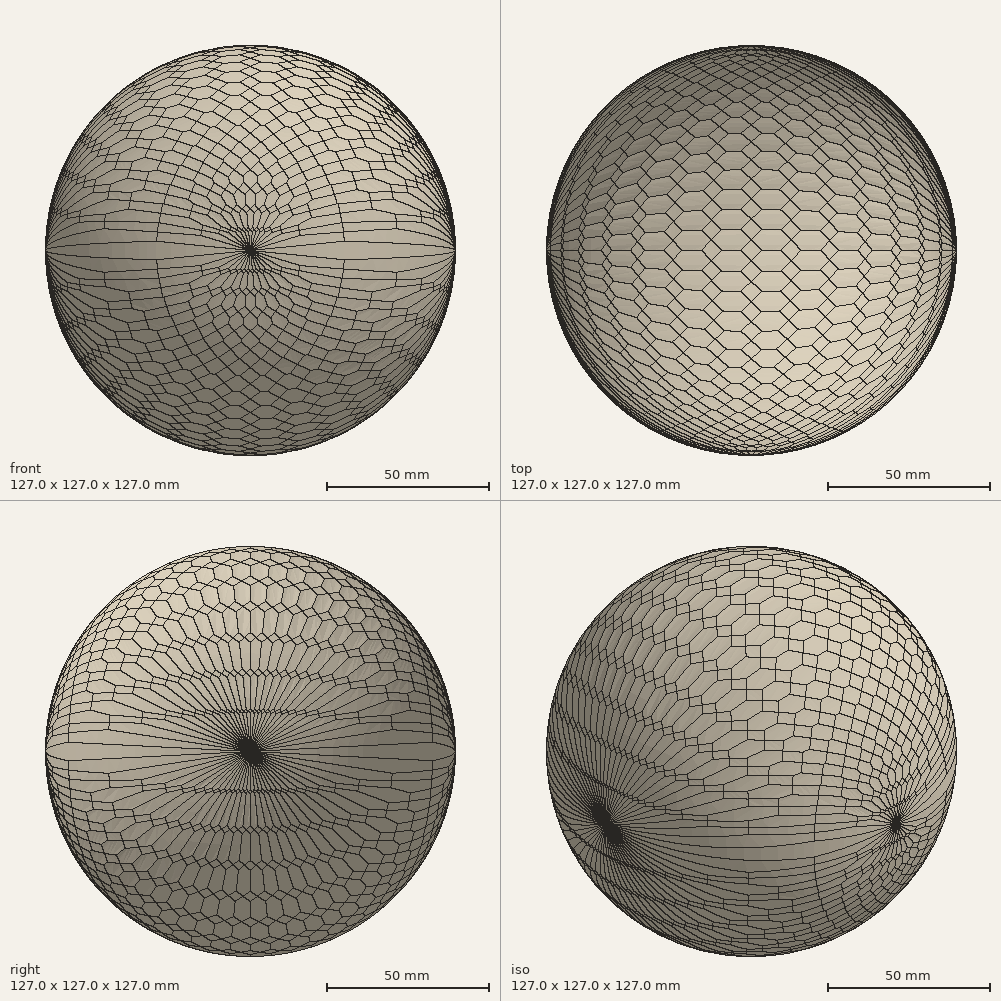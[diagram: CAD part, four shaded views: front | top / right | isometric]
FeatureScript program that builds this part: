
annotation { "Feature Type Name" : "Feature", "Feature Type Description" : "" }
export const myFeature = defineFeature(function(context is Context, id is Id, definition is map)
    precondition{}
    {
        {
            var Q0;
            Q0=qCreatedBy(makeId("Top.planeOp"),FACE);
            var sketch = newSketch(context, id + "F0", { "sketchPlane" : qUnion([Q0])});
            skCircle(sketch, "E0", {"center": v(0, 0) * mm, "radius": 63.5 * mm});
            skLineSegment(sketch, "E1", {"start": v(0, 63.5) * mm, "end": v(0, -63.5) * mm});
            skLineSegment(sketch, "E2", {"start": v(-63.5, 0) * mm, "end": v(63.5, 0) * mm});
            skSolve(sketch);
        }
        {
            var Q0;
            {var subQ0=sQuery(id+"F0.wireOp",EDGE,"E1");var subQ1=sQuery(id+"F0.wireOp",EDGE,"E0");var subQ2=makeQuery(id+"F0.imprint","INTERSECT",VERTEX,{"disambiguationData":[OD(0.0)],"derivedFrom":[subQ1,subQ0]});Q0=makeQuery(id+"F0.imprint","IMPRINT",FACE,{"disambiguationData":[TD([[makeQuery(id+"F0.imprint","IMPRINT",EDGE,{"disambiguationData":[TD([[subQ2,-1.0]])],"derivedFrom":subQ1}),1.0]])]});}
            var Q1;
            {var subQ0=sQuery(id+"F0.wireOp",EDGE,"E1");var subQ1=sQuery(id+"F0.wireOp",EDGE,"E0");var subQ2=makeQuery(id+"F0.imprint","INTERSECT",VERTEX,{"disambiguationData":[OD(0.0)],"derivedFrom":[subQ1,subQ0]});Q1=makeQuery(id+"F0.imprint","IMPRINT",FACE,{"disambiguationData":[TD([[makeQuery(id+"F0.imprint","IMPRINT",EDGE,{"disambiguationData":[TD([[subQ2,1.0]])],"derivedFrom":subQ1}),1.0]])]});}
            var Q2;
            {var subQ0=sQuery(id+"F0.wireOp",EDGE,"E1");var subQ1=sQuery(id+"F0.wireOp",EDGE,"E0");var subQ2=makeQuery(id+"F0.imprint","INTERSECT",VERTEX,{"disambiguationData":[OD(1.0)],"derivedFrom":[subQ1,subQ0]});Q2=makeQuery(id+"F0.imprint","IMPRINT",FACE,{"disambiguationData":[TD([[makeQuery(id+"F0.imprint","IMPRINT",EDGE,{"disambiguationData":[TD([[subQ2,-1.0]])],"derivedFrom":subQ1}),1.0]])]});}
            var Q3;
            {var subQ0=sQuery(id+"F0.wireOp",EDGE,"E1");var subQ1=sQuery(id+"F0.wireOp",EDGE,"E0");var subQ2=makeQuery(id+"F0.imprint","INTERSECT",VERTEX,{"disambiguationData":[OD(1.0)],"derivedFrom":[subQ1,subQ0]});Q3=makeQuery(id+"F0.imprint","IMPRINT",FACE,{"disambiguationData":[TD([[makeQuery(id+"F0.imprint","IMPRINT",EDGE,{"disambiguationData":[TD([[subQ2,1.0]])],"derivedFrom":subQ1}),1.0]])]});}
            extrude(context, id + "F1", {"entities" : qUnion([Q0, Q1, Q2, Q3]), "depth" : 279.4 * mm, "offsetDistance" : 25.4 * mm});
        }
        {
            var Q0;
            Q0=makeQuery(id+"F1.opExtrude","CAP_FACE",FACE,{"disambiguationData":[OSD([sQuery(id+"F0.wireOp",EDGE,"E0")])],"isStart":true});
            extrude(context, id + "F2", {"entities" : qUnion([Q0]), "operationType" : NewBodyOperationType.ADD, "depth" : 279.4 * mm, "offsetDistance" : 25.4 * mm});
        }
        {
            var Q0;
            Q0=makeQuery(id+"F1.opExtrude","SWEPT_BODY",BODY,{"disambiguationData":[OSD([sQuery(id+"F0.wireOp",EDGE,"E0")])]});
            var Q1;
            Q1=sQuery(id+"F0.wireOp",EDGE,"E2");
            circularPattern(context, id + "F3", {"entities" : qUnion([Q0]), "axis" : qUnion([Q1]), "angle" : 180 * degree, "instanceCount" : 32, "equalSpace" : true});
        }
        {
            var Q0;
            Q0=makeQuery(id+"F1.opExtrude","SWEPT_BODY",BODY,{"disambiguationData":[OSD([sQuery(id+"F0.wireOp",EDGE,"E0")])]});
            var Q1;
            Q1=sQuery(id+"F0.wireOp",EDGE,"E1");
            circularPattern(context, id + "F4", {"entities" : qUnion([Q0]), "axis" : qUnion([Q1]), "angle" : 360 * degree, "instanceCount" : 32, "equalSpace" : true});
        }
        {
            var Q0;
            Q0=makeQuery(id+"F1.opExtrude","SWEPT_BODY",BODY,{"disambiguationData":[OSD([sQuery(id+"F0.wireOp",EDGE,"E0")])]});
            var Q1;
            Q1=makeQuery(id+"F3.opPattern","COPY",BODY,{"derivedFrom":makeQuery(id+"F1.opExtrude","SWEPT_BODY",BODY,{"disambiguationData":[OSD([sQuery(id+"F0.wireOp",EDGE,"E0")])]}),"instanceName":"2"});
            var Q2;
            Q2=makeQuery(id+"F3.opPattern","COPY",BODY,{"derivedFrom":makeQuery(id+"F1.opExtrude","SWEPT_BODY",BODY,{"disambiguationData":[OSD([sQuery(id+"F0.wireOp",EDGE,"E0")])]}),"instanceName":"7"});
            var Q3;
            Q3=makeQuery(id+"F3.opPattern","COPY",BODY,{"derivedFrom":makeQuery(id+"F1.opExtrude","SWEPT_BODY",BODY,{"disambiguationData":[OSD([sQuery(id+"F0.wireOp",EDGE,"E0")])]}),"instanceName":"15"});
            var Q4;
            Q4=makeQuery(id+"F4.opPattern","COPY",BODY,{"derivedFrom":makeQuery(id+"F1.opExtrude","SWEPT_BODY",BODY,{"disambiguationData":[OSD([sQuery(id+"F0.wireOp",EDGE,"E0")])]}),"instanceName":"1"});
            var Q5;
            Q5=makeQuery(id+"F4.opPattern","COPY",BODY,{"derivedFrom":makeQuery(id+"F1.opExtrude","SWEPT_BODY",BODY,{"disambiguationData":[OSD([sQuery(id+"F0.wireOp",EDGE,"E0")])]}),"instanceName":"5"});
            var Q6;
            Q6=makeQuery(id+"F4.opPattern","COPY",BODY,{"derivedFrom":makeQuery(id+"F1.opExtrude","SWEPT_BODY",BODY,{"disambiguationData":[OSD([sQuery(id+"F0.wireOp",EDGE,"E0")])]}),"instanceName":"12"});
            var Q7;
            Q7=makeQuery(id+"F4.opPattern","COPY",BODY,{"derivedFrom":makeQuery(id+"F1.opExtrude","SWEPT_BODY",BODY,{"disambiguationData":[OSD([sQuery(id+"F0.wireOp",EDGE,"E0")])]}),"instanceName":"11"});
            var Q8;
            Q8=makeQuery(id+"F4.opPattern","COPY",BODY,{"derivedFrom":makeQuery(id+"F1.opExtrude","SWEPT_BODY",BODY,{"disambiguationData":[OSD([sQuery(id+"F0.wireOp",EDGE,"E0")])]}),"instanceName":"13"});
            var Q9;
            Q9=makeQuery(id+"F4.opPattern","COPY",BODY,{"derivedFrom":makeQuery(id+"F1.opExtrude","SWEPT_BODY",BODY,{"disambiguationData":[OSD([sQuery(id+"F0.wireOp",EDGE,"E0")])]}),"instanceName":"14"});
            var Q10;
            Q10=makeQuery(id+"F4.opPattern","COPY",BODY,{"derivedFrom":makeQuery(id+"F1.opExtrude","SWEPT_BODY",BODY,{"disambiguationData":[OSD([sQuery(id+"F0.wireOp",EDGE,"E0")])]}),"instanceName":"3"});
            var Q11;
            Q11=makeQuery(id+"F4.opPattern","COPY",BODY,{"derivedFrom":makeQuery(id+"F1.opExtrude","SWEPT_BODY",BODY,{"disambiguationData":[OSD([sQuery(id+"F0.wireOp",EDGE,"E0")])]}),"instanceName":"6"});
            var Q12;
            Q12=makeQuery(id+"F4.opPattern","COPY",BODY,{"derivedFrom":makeQuery(id+"F1.opExtrude","SWEPT_BODY",BODY,{"disambiguationData":[OSD([sQuery(id+"F0.wireOp",EDGE,"E0")])]}),"instanceName":"8"});
            var Q13;
            Q13=makeQuery(id+"F4.opPattern","COPY",BODY,{"derivedFrom":makeQuery(id+"F1.opExtrude","SWEPT_BODY",BODY,{"disambiguationData":[OSD([sQuery(id+"F0.wireOp",EDGE,"E0")])]}),"instanceName":"7"});
            var Q14;
            Q14=makeQuery(id+"F4.opPattern","COPY",BODY,{"derivedFrom":makeQuery(id+"F1.opExtrude","SWEPT_BODY",BODY,{"disambiguationData":[OSD([sQuery(id+"F0.wireOp",EDGE,"E0")])]}),"instanceName":"4"});
            var Q15;
            Q15=makeQuery(id+"F3.opPattern","COPY",BODY,{"derivedFrom":makeQuery(id+"F1.opExtrude","SWEPT_BODY",BODY,{"disambiguationData":[OSD([sQuery(id+"F0.wireOp",EDGE,"E0")])]}),"instanceName":"13"});
            var Q16;
            Q16=makeQuery(id+"F3.opPattern","COPY",BODY,{"derivedFrom":makeQuery(id+"F1.opExtrude","SWEPT_BODY",BODY,{"disambiguationData":[OSD([sQuery(id+"F0.wireOp",EDGE,"E0")])]}),"instanceName":"14"});
            var Q17;
            Q17=makeQuery(id+"F3.opPattern","COPY",BODY,{"derivedFrom":makeQuery(id+"F1.opExtrude","SWEPT_BODY",BODY,{"disambiguationData":[OSD([sQuery(id+"F0.wireOp",EDGE,"E0")])]}),"instanceName":"12"});
            var Q18;
            Q18=makeQuery(id+"F3.opPattern","COPY",BODY,{"derivedFrom":makeQuery(id+"F1.opExtrude","SWEPT_BODY",BODY,{"disambiguationData":[OSD([sQuery(id+"F0.wireOp",EDGE,"E0")])]}),"instanceName":"11"});
            var Q19;
            Q19=makeQuery(id+"F4.opPattern","COPY",BODY,{"derivedFrom":makeQuery(id+"F1.opExtrude","SWEPT_BODY",BODY,{"disambiguationData":[OSD([sQuery(id+"F0.wireOp",EDGE,"E0")])]}),"instanceName":"10"});
            var Q20;
            Q20=makeQuery(id+"F3.opPattern","COPY",BODY,{"derivedFrom":makeQuery(id+"F1.opExtrude","SWEPT_BODY",BODY,{"disambiguationData":[OSD([sQuery(id+"F0.wireOp",EDGE,"E0")])]}),"instanceName":"20"});
            var Q21;
            Q21=makeQuery(id+"F3.opPattern","COPY",BODY,{"derivedFrom":makeQuery(id+"F1.opExtrude","SWEPT_BODY",BODY,{"disambiguationData":[OSD([sQuery(id+"F0.wireOp",EDGE,"E0")])]}),"instanceName":"18"});
            var Q22;
            Q22=makeQuery(id+"F3.opPattern","COPY",BODY,{"derivedFrom":makeQuery(id+"F1.opExtrude","SWEPT_BODY",BODY,{"disambiguationData":[OSD([sQuery(id+"F0.wireOp",EDGE,"E0")])]}),"instanceName":"17"});
            var Q23;
            Q23=makeQuery(id+"F3.opPattern","COPY",BODY,{"derivedFrom":makeQuery(id+"F1.opExtrude","SWEPT_BODY",BODY,{"disambiguationData":[OSD([sQuery(id+"F0.wireOp",EDGE,"E0")])]}),"instanceName":"21"});
            var Q24;
            Q24=makeQuery(id+"F4.opPattern","COPY",BODY,{"derivedFrom":makeQuery(id+"F1.opExtrude","SWEPT_BODY",BODY,{"disambiguationData":[OSD([sQuery(id+"F0.wireOp",EDGE,"E0")])]}),"instanceName":"16"});
            var Q25;
            Q25=makeQuery(id+"F4.opPattern","COPY",BODY,{"derivedFrom":makeQuery(id+"F1.opExtrude","SWEPT_BODY",BODY,{"disambiguationData":[OSD([sQuery(id+"F0.wireOp",EDGE,"E0")])]}),"instanceName":"24"});
            var Q26;
            Q26=makeQuery(id+"F4.opPattern","COPY",BODY,{"derivedFrom":makeQuery(id+"F1.opExtrude","SWEPT_BODY",BODY,{"disambiguationData":[OSD([sQuery(id+"F0.wireOp",EDGE,"E0")])]}),"instanceName":"28"});
            var Q27;
            Q27=makeQuery(id+"F4.opPattern","COPY",BODY,{"derivedFrom":makeQuery(id+"F1.opExtrude","SWEPT_BODY",BODY,{"disambiguationData":[OSD([sQuery(id+"F0.wireOp",EDGE,"E0")])]}),"instanceName":"27"});
            var Q28;
            Q28=makeQuery(id+"F4.opPattern","COPY",BODY,{"derivedFrom":makeQuery(id+"F1.opExtrude","SWEPT_BODY",BODY,{"disambiguationData":[OSD([sQuery(id+"F0.wireOp",EDGE,"E0")])]}),"instanceName":"20"});
            var Q29;
            Q29=makeQuery(id+"F3.opPattern","COPY",BODY,{"derivedFrom":makeQuery(id+"F1.opExtrude","SWEPT_BODY",BODY,{"disambiguationData":[OSD([sQuery(id+"F0.wireOp",EDGE,"E0")])]}),"instanceName":"27"});
            var Q30;
            Q30=makeQuery(id+"F4.opPattern","COPY",BODY,{"derivedFrom":makeQuery(id+"F1.opExtrude","SWEPT_BODY",BODY,{"disambiguationData":[OSD([sQuery(id+"F0.wireOp",EDGE,"E0")])]}),"instanceName":"31"});
            var Q31;
            Q31=makeQuery(id+"F4.opPattern","COPY",BODY,{"derivedFrom":makeQuery(id+"F1.opExtrude","SWEPT_BODY",BODY,{"disambiguationData":[OSD([sQuery(id+"F0.wireOp",EDGE,"E0")])]}),"instanceName":"30"});
            var Q32;
            Q32=makeQuery(id+"F4.opPattern","COPY",BODY,{"derivedFrom":makeQuery(id+"F1.opExtrude","SWEPT_BODY",BODY,{"disambiguationData":[OSD([sQuery(id+"F0.wireOp",EDGE,"E0")])]}),"instanceName":"25"});
            var Q33;
            Q33=makeQuery(id+"F4.opPattern","COPY",BODY,{"derivedFrom":makeQuery(id+"F1.opExtrude","SWEPT_BODY",BODY,{"disambiguationData":[OSD([sQuery(id+"F0.wireOp",EDGE,"E0")])]}),"instanceName":"18"});
            var Q34;
            Q34=makeQuery(id+"F3.opPattern","COPY",BODY,{"derivedFrom":makeQuery(id+"F1.opExtrude","SWEPT_BODY",BODY,{"disambiguationData":[OSD([sQuery(id+"F0.wireOp",EDGE,"E0")])]}),"instanceName":"24"});
            var Q35;
            Q35=makeQuery(id+"F4.opPattern","COPY",BODY,{"derivedFrom":makeQuery(id+"F1.opExtrude","SWEPT_BODY",BODY,{"disambiguationData":[OSD([sQuery(id+"F0.wireOp",EDGE,"E0")])]}),"instanceName":"21"});
            var Q36;
            Q36=makeQuery(id+"F4.opPattern","COPY",BODY,{"derivedFrom":makeQuery(id+"F1.opExtrude","SWEPT_BODY",BODY,{"disambiguationData":[OSD([sQuery(id+"F0.wireOp",EDGE,"E0")])]}),"instanceName":"23"});
            var Q37;
            Q37=makeQuery(id+"F4.opPattern","COPY",BODY,{"derivedFrom":makeQuery(id+"F1.opExtrude","SWEPT_BODY",BODY,{"disambiguationData":[OSD([sQuery(id+"F0.wireOp",EDGE,"E0")])]}),"instanceName":"22"});
            var Q38;
            Q38=makeQuery(id+"F3.opPattern","COPY",BODY,{"derivedFrom":makeQuery(id+"F1.opExtrude","SWEPT_BODY",BODY,{"disambiguationData":[OSD([sQuery(id+"F0.wireOp",EDGE,"E0")])]}),"instanceName":"22"});
            var Q39;
            Q39=makeQuery(id+"F3.opPattern","COPY",BODY,{"derivedFrom":makeQuery(id+"F1.opExtrude","SWEPT_BODY",BODY,{"disambiguationData":[OSD([sQuery(id+"F0.wireOp",EDGE,"E0")])]}),"instanceName":"16"});
            var Q40;
            Q40=makeQuery(id+"F3.opPattern","COPY",BODY,{"derivedFrom":makeQuery(id+"F1.opExtrude","SWEPT_BODY",BODY,{"disambiguationData":[OSD([sQuery(id+"F0.wireOp",EDGE,"E0")])]}),"instanceName":"23"});
            var Q41;
            Q41=makeQuery(id+"F3.opPattern","COPY",BODY,{"derivedFrom":makeQuery(id+"F1.opExtrude","SWEPT_BODY",BODY,{"disambiguationData":[OSD([sQuery(id+"F0.wireOp",EDGE,"E0")])]}),"instanceName":"25"});
            var Q42;
            Q42=makeQuery(id+"F3.opPattern","COPY",BODY,{"derivedFrom":makeQuery(id+"F1.opExtrude","SWEPT_BODY",BODY,{"disambiguationData":[OSD([sQuery(id+"F0.wireOp",EDGE,"E0")])]}),"instanceName":"30"});
            var Q43;
            Q43=makeQuery(id+"F4.opPattern","COPY",BODY,{"derivedFrom":makeQuery(id+"F1.opExtrude","SWEPT_BODY",BODY,{"disambiguationData":[OSD([sQuery(id+"F0.wireOp",EDGE,"E0")])]}),"instanceName":"26"});
            var Q44;
            Q44=makeQuery(id+"F4.opPattern","COPY",BODY,{"derivedFrom":makeQuery(id+"F1.opExtrude","SWEPT_BODY",BODY,{"disambiguationData":[OSD([sQuery(id+"F0.wireOp",EDGE,"E0")])]}),"instanceName":"9"});
            var Q45;
            Q45=makeQuery(id+"F4.opPattern","COPY",BODY,{"derivedFrom":makeQuery(id+"F1.opExtrude","SWEPT_BODY",BODY,{"disambiguationData":[OSD([sQuery(id+"F0.wireOp",EDGE,"E0")])]}),"instanceName":"29"});
            var Q46;
            Q46=makeQuery(id+"F4.opPattern","COPY",BODY,{"derivedFrom":makeQuery(id+"F1.opExtrude","SWEPT_BODY",BODY,{"disambiguationData":[OSD([sQuery(id+"F0.wireOp",EDGE,"E0")])]}),"instanceName":"19"});
            var Q47;
            Q47=makeQuery(id+"F4.opPattern","COPY",BODY,{"derivedFrom":makeQuery(id+"F1.opExtrude","SWEPT_BODY",BODY,{"disambiguationData":[OSD([sQuery(id+"F0.wireOp",EDGE,"E0")])]}),"instanceName":"17"});
            var Q48;
            Q48=makeQuery(id+"F3.opPattern","COPY",BODY,{"derivedFrom":makeQuery(id+"F1.opExtrude","SWEPT_BODY",BODY,{"disambiguationData":[OSD([sQuery(id+"F0.wireOp",EDGE,"E0")])]}),"instanceName":"4"});
            var Q49;
            Q49=makeQuery(id+"F3.opPattern","COPY",BODY,{"derivedFrom":makeQuery(id+"F1.opExtrude","SWEPT_BODY",BODY,{"disambiguationData":[OSD([sQuery(id+"F0.wireOp",EDGE,"E0")])]}),"instanceName":"19"});
            var Q50;
            Q50=makeQuery(id+"F3.opPattern","COPY",BODY,{"derivedFrom":makeQuery(id+"F1.opExtrude","SWEPT_BODY",BODY,{"disambiguationData":[OSD([sQuery(id+"F0.wireOp",EDGE,"E0")])]}),"instanceName":"26"});
            var Q51;
            Q51=makeQuery(id+"F3.opPattern","COPY",BODY,{"derivedFrom":makeQuery(id+"F1.opExtrude","SWEPT_BODY",BODY,{"disambiguationData":[OSD([sQuery(id+"F0.wireOp",EDGE,"E0")])]}),"instanceName":"9"});
            var Q52;
            Q52=makeQuery(id+"F3.opPattern","COPY",BODY,{"derivedFrom":makeQuery(id+"F1.opExtrude","SWEPT_BODY",BODY,{"disambiguationData":[OSD([sQuery(id+"F0.wireOp",EDGE,"E0")])]}),"instanceName":"31"});
            var Q53;
            Q53=makeQuery(id+"F3.opPattern","COPY",BODY,{"derivedFrom":makeQuery(id+"F1.opExtrude","SWEPT_BODY",BODY,{"disambiguationData":[OSD([sQuery(id+"F0.wireOp",EDGE,"E0")])]}),"instanceName":"5"});
            var Q54;
            Q54=makeQuery(id+"F3.opPattern","COPY",BODY,{"derivedFrom":makeQuery(id+"F1.opExtrude","SWEPT_BODY",BODY,{"disambiguationData":[OSD([sQuery(id+"F0.wireOp",EDGE,"E0")])]}),"instanceName":"8"});
            var Q55;
            Q55=makeQuery(id+"F3.opPattern","COPY",BODY,{"derivedFrom":makeQuery(id+"F1.opExtrude","SWEPT_BODY",BODY,{"disambiguationData":[OSD([sQuery(id+"F0.wireOp",EDGE,"E0")])]}),"instanceName":"10"});
            var Q56;
            Q56=makeQuery(id+"F3.opPattern","COPY",BODY,{"derivedFrom":makeQuery(id+"F1.opExtrude","SWEPT_BODY",BODY,{"disambiguationData":[OSD([sQuery(id+"F0.wireOp",EDGE,"E0")])]}),"instanceName":"6"});
            var Q57;
            Q57=makeQuery(id+"F4.opPattern","COPY",BODY,{"derivedFrom":makeQuery(id+"F1.opExtrude","SWEPT_BODY",BODY,{"disambiguationData":[OSD([sQuery(id+"F0.wireOp",EDGE,"E0")])]}),"instanceName":"15"});
            var Q58;
            Q58=makeQuery(id+"F3.opPattern","COPY",BODY,{"derivedFrom":makeQuery(id+"F1.opExtrude","SWEPT_BODY",BODY,{"disambiguationData":[OSD([sQuery(id+"F0.wireOp",EDGE,"E0")])]}),"instanceName":"3"});
            var Q59;
            Q59=makeQuery(id+"F3.opPattern","COPY",BODY,{"derivedFrom":makeQuery(id+"F1.opExtrude","SWEPT_BODY",BODY,{"disambiguationData":[OSD([sQuery(id+"F0.wireOp",EDGE,"E0")])]}),"instanceName":"28"});
            var Q60;
            Q60=makeQuery(id+"F3.opPattern","COPY",BODY,{"derivedFrom":makeQuery(id+"F1.opExtrude","SWEPT_BODY",BODY,{"disambiguationData":[OSD([sQuery(id+"F0.wireOp",EDGE,"E0")])]}),"instanceName":"29"});
            var Q61;
            Q61=makeQuery(id+"F3.opPattern","COPY",BODY,{"derivedFrom":makeQuery(id+"F1.opExtrude","SWEPT_BODY",BODY,{"disambiguationData":[OSD([sQuery(id+"F0.wireOp",EDGE,"E0")])]}),"instanceName":"1"});
            var Q62;
            Q62=makeQuery(id+"F4.opPattern","COPY",BODY,{"derivedFrom":makeQuery(id+"F1.opExtrude","SWEPT_BODY",BODY,{"disambiguationData":[OSD([sQuery(id+"F0.wireOp",EDGE,"E0")])]}),"instanceName":"2"});
            booleanBodies(context, id + "F5", {"operationType" : BooleanOperationType.INTERSECTION, "tools" : qUnion([Q0, Q1, Q2, Q3, Q4, Q5, Q6, Q7, Q8, Q9, Q10, Q11, Q12, Q13, Q14, Q15, Q16, Q17, Q18, Q19, Q20, Q21, Q22, Q23, Q24, Q25, Q26, Q27, Q28, Q29, Q30, Q31, Q32, Q33, Q34, Q35, Q36, Q37, Q38, Q39, Q40, Q41, Q42, Q43, Q44, Q45, Q46, Q47, Q48, Q49, Q50, Q51, Q52, Q53, Q54, Q55, Q56, Q57, Q58, Q59, Q60, Q61, Q62])});
        }
    });
